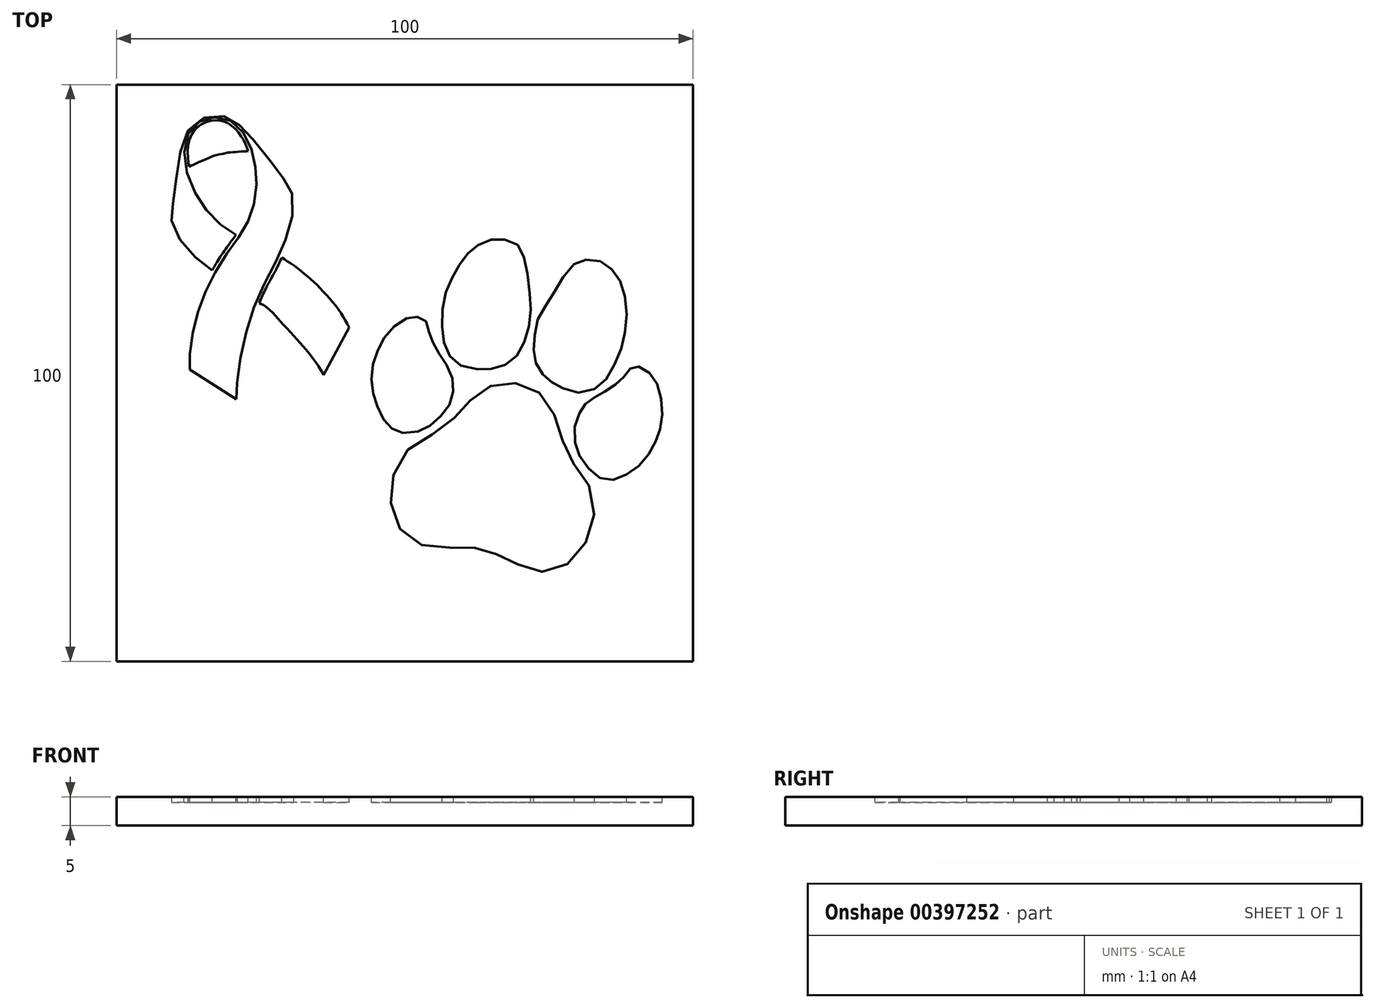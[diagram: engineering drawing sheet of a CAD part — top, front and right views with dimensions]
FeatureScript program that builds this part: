
annotation { "Feature Type Name" : "Feature", "Feature Type Description" : "" }
export const myFeature = defineFeature(function(context is Context, id is Id, definition is map)
    precondition{}
    {
        {
            var Q0;
            Q0=qCreatedBy(makeId("Top.planeOp"),FACE);
            var sketch = newSketch(context, id + "F0", { "sketchPlane" : qUnion([Q0])});
            skLineSegment(sketch, "E0.bottom", {"start": v(0, 0) * mm, "end": v(-100, 0) * mm});
            skLineSegment(sketch, "E0.top", {"start": v(0, 100) * mm, "end": v(-100, 100) * mm});
            skLineSegment(sketch, "E0.left", {"start": v(0, 0) * mm, "end": v(0, 100) * mm});
            skLineSegment(sketch, "E0.right", {"start": v(-100, 0) * mm, "end": v(-100, 100) * mm});
            skSolve(sketch);
        }
        {
            var Q0;
            Q0 = qSketchRegion(id + "F0", true);
            extrude(context, id + "F1", {"entities" : qUnion([Q0]), "depth" : 5 * mm});
        }
        {
            var Q0;
            Q0=makeQuery(id+"F1.opExtrude","CAP_FACE",FACE,{"disambiguationData":[OSD([sQuery(id+"F0.wireOp",EDGE,"E0.bottom"),sQuery(id+"F0.wireOp",EDGE,"E0.top"),sQuery(id+"F0.wireOp",EDGE,"E0.left"),sQuery(id+"F0.wireOp",EDGE,"E0.right")])],"isStart":false});
            var sketch = newSketch(context, id + "F2", { "sketchPlane" : qUnion([Q0])});
            skFitSpline(sketch, "E1", {"points": [v(-50.29, 39.62) * mm, v(-51.72, 39.96) * mm, v(-52.71, 40.84) * mm, v(-53.7, 41.94) * mm, v(-54.59, 43.82) * mm, v(-55.14, 45.36) * mm, v(-55.58, 46.9) * mm, v(-55.8, 49) * mm, v(-55.58, 51.1) * mm, v(-55.03, 53.09) * mm, v(-54.26, 54.85) * mm, v(-53.15, 56.62) * mm, v(-51.72, 58.17) * mm, v(-49.95, 59.38) * mm, v(-48.63, 59.71) * mm, v(-47.75, 59.71) * mm, v(-46.75, 59.38) * mm, v(-46.2, 58.72) * mm, v(-45.87, 57.61) * mm, v(-45.65, 56.4) * mm, v(-45.1, 55.3) * mm, v(-44.33, 53.86) * mm, v(-43.55, 52.65) * mm, v(-42.56, 51.1) * mm, v(-41.79, 49.23) * mm, v(-41.57, 47.57) * mm, v(-41.79, 45.92) * mm, v(-42.45, 44.15) * mm, v(-43.66, 42.6) * mm, v(-44.99, 41.28) * mm, v(-46.75, 40.29) * mm, v(-48.08, 39.73) * mm, v(-50.29, 39.62) * mm]});
            skFitSpline(sketch, "E2", {"points": [v(-37.37, 50.66) * mm, v(-35.83, 50.55) * mm, v(-34.5, 50.88) * mm, v(-32.85, 51.32) * mm, v(-31.41, 52.2) * mm, v(-30.09, 53.53) * mm, v(-29.32, 55.3) * mm, v(-28.65, 57.28) * mm, v(-28.21, 59.5) * mm, v(-28.21, 61.7) * mm, v(-28.32, 63.8) * mm, v(-28.65, 66.88) * mm, v(-29.1, 69.1) * mm, v(-29.76, 71.41) * mm, v(-30.42, 72.18) * mm, v(-31.74, 72.96) * mm, v(-33.29, 73.18) * mm, v(-34.72, 73.18) * mm, v(-36.27, 72.73) * mm, v(-37.6, 71.96) * mm, v(-38.7, 71.08) * mm, v(-39.69, 69.98) * mm, v(-40.57, 68.65) * mm, v(-41.35, 67.22) * mm, v(-42.34, 65.45) * mm, v(-43, 63.57) * mm, v(-43.44, 61.37) * mm, v(-43.55, 58.83) * mm, v(-43.44, 56.73) * mm, v(-43.11, 54.74) * mm, v(-42.45, 53.2) * mm, v(-41.12, 51.87) * mm, v(-39.8, 51.1) * mm, v(-37.37, 50.66) * mm]});
            skFitSpline(sketch, "E3", {"points": [v(-24.57, 48.45) * mm, v(-25.56, 49.23) * mm, v(-26.67, 50.66) * mm, v(-27.44, 52.2) * mm, v(-27.66, 54.2) * mm, v(-27.44, 56.51) * mm, v(-27, 59.05) * mm, v(-25.78, 61.37) * mm, v(-24.24, 63.8) * mm, v(-22.8, 66.22) * mm, v(-20.82, 68.76) * mm, v(-19.27, 69.53) * mm, v(-17.17, 69.64) * mm, v(-15.19, 68.87) * mm, v(-13.75, 67.55) * mm, v(-12.54, 65.67) * mm, v(-11.77, 62.91) * mm, v(-11.55, 59.5) * mm, v(-11.99, 56.07) * mm, v(-12.76, 53.42) * mm, v(-14.08, 50.66) * mm, v(-15.63, 48.23) * mm, v(-17.84, 46.9) * mm, v(-20.7, 46.69) * mm, v(-23.02, 47.57) * mm, v(-24.57, 48.45) * mm]});
            skFitSpline(sketch, "E4", {"points": [v(-19.71, 43.05) * mm, v(-20.38, 41.28) * mm, v(-20.6, 38.96) * mm, v(-20.15, 36.86) * mm, v(-19.5, 35.2) * mm, v(-17.95, 33.22) * mm, v(-16.4, 31.9) * mm, v(-14.86, 31.46) * mm, v(-12.98, 31.68) * mm, v(-11.1, 32.67) * mm, v(-9.45, 33.89) * mm, v(-8.01, 35.54) * mm, v(-6.8, 37.42) * mm, v(-6.25, 38.85) * mm, v(-5.7, 40.5) * mm, v(-5.37, 42.6) * mm, v(-5.48, 44.81) * mm, v(-5.92, 47.24) * mm, v(-6.8, 49) * mm, v(-7.8, 50.22) * mm, v(-9.17, 51.04) * mm, v(-9.89, 51.17) * mm, v(-10.6, 50.97) * mm, v(-11.4, 50.05) * mm, v(-11.99, 49.33) * mm, v(-12.64, 48.67) * mm, v(-13.9, 47.69) * mm, v(-15.2, 46.84) * mm, v(-16.38, 46.18) * mm, v(-17.43, 45.52) * mm, v(-18.42, 44.8) * mm, v(-19.14, 44.08) * mm, v(-19.71, 43.05) * mm]});
            skFitSpline(sketch, "E5", {"points": [v(-37.84, 19.69) * mm, v(-36.65, 19.43) * mm, v(-35.2, 18.92) * mm, v(-33.67, 18.41) * mm, v(-32.14, 17.65) * mm, v(-30.77, 16.96) * mm, v(-29.24, 16.28) * mm, v(-27.8, 15.77) * mm, v(-25.58, 15.52) * mm, v(-23.54, 15.94) * mm, v(-21.84, 16.88) * mm, v(-20.14, 18.33) * mm, v(-18.86, 20.2) * mm, v(-17.75, 22.84) * mm, v(-17.24, 24.88) * mm, v(-17.16, 27.43) * mm, v(-17.75, 29.73) * mm, v(-18.86, 31.77) * mm, v(-20.14, 33.47) * mm, v(-21.07, 34.75) * mm, v(-21.92, 36.37) * mm, v(-22.6, 38.24) * mm, v(-23.29, 40.54) * mm, v(-23.88, 42.24) * mm, v(-24.73, 44.2) * mm, v(-25.84, 45.82) * mm, v(-27.54, 47.18) * mm, v(-29.24, 47.94) * mm, v(-31.03, 48.28) * mm, v(-32.65, 48.37) * mm, v(-34.52, 47.94) * mm, v(-36.48, 47.18) * mm, v(-37.84, 46.07) * mm, v(-38.86, 44.96) * mm, v(-40.05, 43.69) * mm, v(-41.07, 42.58) * mm, v(-42.43, 41.3) * mm, v(-44.4, 39.86) * mm, v(-46, 39) * mm, v(-48.14, 37.82) * mm, v(-50.1, 35.94) * mm, v(-51.54, 33.65) * mm, v(-52.05, 31.86) * mm, v(-52.48, 29.48) * mm, v(-52.4, 27.43) * mm, v(-51.97, 25.4) * mm, v(-51.03, 23.26) * mm, v(-49.5, 21.65) * mm, v(-47.8, 20.45) * mm, v(-45.92, 19.86) * mm, v(-43.8, 19.69) * mm, v(-41.41, 19.77) * mm, v(-39.88, 19.94) * mm, v(-37.84, 19.69) * mm]});
            skLineSegment(sketch, "E6", {"start": v(-87.27, 50.56) * mm, "end": v(-79.23, 45.45) * mm});
            skFitSpline(sketch, "E7", {"points": [v(-87.4, 85.74) * mm, v(-87.52, 86.56) * mm, v(-87.64, 87.89) * mm, v(-87.56, 89.49) * mm, v(-87.13, 90.97) * mm, v(-86.58, 91.95) * mm, v(-85.96, 92.6) * mm, v(-85.22, 93.16) * mm, v(-84.24, 93.55) * mm, v(-83.23, 93.78) * mm, v(-82.02, 93.74) * mm, v(-81.12, 93.5) * mm, v(-80.38, 93.16) * mm, v(-79.75, 92.65) * mm, v(-79.09, 92.02) * mm, v(-78.47, 91.2) * mm, v(-77.96, 90.42) * mm, v(-77.57, 89.6) * mm, v(-77.37, 89.06) * mm, v(-77.18, 88.47) * mm], "startDerivative": vector(-2.44, 16.03) * mm, "endDerivative": vector(4.8, -14.41) * mm});
            skFitSpline(sketch, "E8", {"points": [v(-87.4, 85.74) * mm, v(-86.82, 86.05) * mm, v(-85.88, 86.48) * mm, v(-84.7, 87) * mm, v(-83.81, 87.38) * mm, v(-82.84, 87.73) * mm, v(-81.63, 88) * mm, v(-80.57, 88.24) * mm, v(-79.75, 88.28) * mm, v(-78.66, 88.4) * mm, v(-77.72, 88.43) * mm, v(-77.18, 88.47) * mm], "startDerivative": vector(7.32, 4.06) * mm, "endDerivative": vector(7.46, 0.67) * mm});
            skFitSpline(sketch, "E9", {"points": [v(-79.3, 73.96) * mm, v(-80.1, 74.36) * mm, v(-81.48, 75.33) * mm, v(-83.1, 76.74) * mm, v(-84.16, 77.9) * mm, v(-84.97, 78.97) * mm, v(-85.93, 80.49) * mm, v(-87.04, 82.56) * mm, v(-87.65, 84.33) * mm, v(-88.16, 86.36) * mm, v(-88.26, 87.98) * mm, v(-88.16, 89.6) * mm, v(-87.75, 91.01) * mm, v(-87.04, 92.38) * mm, v(-86.23, 93.14) * mm, v(-85.52, 93.64) * mm, v(-84.46, 94.1) * mm, v(-83.5, 94.3) * mm, v(-82.44, 94.35) * mm, v(-81.22, 94.15) * mm, v(-80.16, 93.75) * mm, v(-79.15, 92.99) * mm, v(-78.34, 92.08) * mm, v(-77.58, 90.96) * mm, v(-76.92, 89.75) * mm, v(-76.42, 88.23) * mm, v(-76.06, 86.66) * mm, v(-75.86, 85.4) * mm, v(-75.76, 84.23) * mm, v(-75.7, 82.81) * mm, v(-75.8, 81.3) * mm, v(-76.08, 79.66) * mm, v(-76.47, 78.14) * mm, v(-76.82, 77.04) * mm, v(-77.6, 75.45) * mm, v(-78.3, 74.24) * mm, v(-79.1, 73.13) * mm, v(-80.12, 71.76) * mm, v(-81.18, 70.3) * mm, v(-82.3, 68.52) * mm, v(-83.26, 66.7) * mm, v(-84.12, 65.03) * mm, v(-84.98, 63.06) * mm, v(-85.64, 61.18) * mm, v(-86.2, 59.41) * mm, v(-86.65, 57.6) * mm, v(-87, 55.52) * mm, v(-87.2, 53.8) * mm, v(-87.3, 52.14) * mm, v(-87.28, 51) * mm, v(-87.27, 50.56) * mm], "startDerivative": vector(-49.75, 22.47) * mm, "endDerivative": vector(0.94, -36.49) * mm});
            skFitSpline(sketch, "E10", {"points": [v(-79.3, 73.96) * mm, v(-79.8, 73.24) * mm, v(-80.03, 72.94) * mm, v(-80.38, 72.47) * mm, v(-80.96, 71.62) * mm, v(-81.72, 70.55) * mm, v(-82.42, 69.46) * mm, v(-82.85, 68.73) * mm, v(-83.14, 68.27) * mm, v(-83.4, 67.79) * mm], "startDerivative": vector(-4.69, -6.92) * mm, "endDerivative": vector(-2.87, -5.31) * mm});
            skFitSpline(sketch, "E11", {"points": [v(-83.4, 67.79) * mm, v(-84.54, 68.57) * mm, v(-86.16, 69.89) * mm, v(-87.98, 71.76) * mm, v(-89, 73.13) * mm, v(-89.9, 74.8) * mm, v(-90.4, 76.37) * mm, v(-90.46, 77.12) * mm, v(-90.3, 78.29) * mm, v(-90.1, 80.06) * mm, v(-89.8, 82.44) * mm, v(-89.4, 85.47) * mm, v(-88.94, 88.1) * mm, v(-88.49, 89.93) * mm, v(-87.63, 91.95) * mm, v(-86.61, 93.27) * mm, v(-84.98, 94.18) * mm, v(-83.4, 94.58) * mm, v(-81.86, 94.63) * mm, v(-80.54, 94.28) * mm, v(-79.53, 93.72) * mm, v(-78.47, 92.81) * mm, v(-77.5, 91.85) * mm, v(-76.19, 90.38) * mm, v(-74.32, 88.05) * mm, v(-73, 86.33) * mm, v(-71.63, 84.51) * mm, v(-70.77, 83.35) * mm, v(-69.96, 82.18) * mm, v(-69.61, 81.22) * mm, v(-69.36, 79.76) * mm, v(-69.46, 77.43) * mm, v(-70.02, 75) * mm, v(-70.88, 72.62) * mm, v(-71.74, 70.55) * mm, v(-72.65, 68.77) * mm, v(-73.91, 66.3) * mm, v(-75.18, 63.77) * mm, v(-76.04, 61.74) * mm, v(-76.9, 59.1) * mm, v(-77.57, 56.75) * mm, v(-78.27, 53.98) * mm, v(-78.77, 51.1) * mm, v(-79.1, 48.73) * mm, v(-79.1, 47.57) * mm, v(-79.18, 46.76) * mm, v(-79.23, 45.45) * mm], "startDerivative": vector(-59.22, 40.03) * mm, "endDerivative": vector(-0.04, -77.87) * mm});
            skLineSegment(sketch, "E12", {"start": v(-64.08, 49.64) * mm, "end": v(-59.66, 57.9) * mm});
            skFitSpline(sketch, "E13", {"points": [v(-64.08, 49.64) * mm, v(-64.85, 51) * mm, v(-67.06, 53.98) * mm, v(-68.94, 56.1) * mm, v(-71.4, 58.75) * mm, v(-72.77, 60.28) * mm, v(-74.47, 61.72) * mm, v(-75.23, 62.15) * mm], "startDerivative": vector(-5.18, 10.26) * mm, "endDerivative": vector(-5.94, 5.26) * mm});
            skFitSpline(sketch, "E14", {"points": [v(-59.66, 57.9) * mm, v(-60.6, 59.6) * mm, v(-61.79, 61.38) * mm, v(-63.57, 63.51) * mm, v(-65.2, 65.21) * mm, v(-66.9, 66.75) * mm, v(-68.51, 68.1) * mm, v(-70.13, 69.21) * mm, v(-71.32, 70) * mm], "startDerivative": vector(-7.58, 14.27) * mm, "endDerivative": vector(-11.08, 7.4) * mm});
            skFitSpline(sketch, "E15", {"points": [v(-71.32, 70) * mm, v(-71.68, 69.28) * mm, v(-72.04, 68.5) * mm, v(-72.67, 67.27) * mm, v(-73.18, 66.33) * mm, v(-73.82, 65.22) * mm, v(-74.27, 64.32) * mm, v(-74.63, 63.56) * mm, v(-74.93, 62.87) * mm, v(-75.23, 62.15) * mm], "startDerivative": vector(-3.64, -7.1) * mm, "endDerivative": vector(-1.08, -6.91) * mm});
            skSolve(sketch);
        }
        {
            var Q0;
            Q0=makeQuery(id+"F2.imprint","IMPRINT",FACE,{"disambiguationData":[TD([[makeQuery(id+"F2.imprint","IMPRINT",EDGE,{"derivedFrom":sQuery(id+"F2.wireOp",EDGE,"E12")}),1.0]])]});
            var Q1;
            Q1=makeQuery(id+"F2.imprint","IMPRINT",FACE,{"disambiguationData":[TD([[makeQuery(id+"F2.imprint","IMPRINT",EDGE,{"derivedFrom":sQuery(id+"F2.wireOp",EDGE,"E6")}),1.0]])]});
            var Q2;
            Q2=makeQuery(id+"F2.imprint","IMPRINT",FACE,{"disambiguationData":[TD([[makeQuery(id+"F2.imprint","IMPRINT",EDGE,{"derivedFrom":sQuery(id+"F2.wireOp",EDGE,"E7")}),-1.0]])]});
            var Q3;
            Q3=makeQuery(id+"F2.imprint","IMPRINT",FACE,{"disambiguationData":[TD([[makeQuery(id+"F2.imprint","IMPRINT",EDGE,{"derivedFrom":sQuery(id+"F2.wireOp",EDGE,"E1")}),-1.0]])]});
            var Q4;
            Q4=makeQuery(id+"F2.imprint","IMPRINT",FACE,{"disambiguationData":[TD([[makeQuery(id+"F2.imprint","IMPRINT",EDGE,{"derivedFrom":sQuery(id+"F2.wireOp",EDGE,"E2")}),1.0]])]});
            var Q5;
            Q5=makeQuery(id+"F2.imprint","IMPRINT",FACE,{"disambiguationData":[TD([[makeQuery(id+"F2.imprint","IMPRINT",EDGE,{"derivedFrom":sQuery(id+"F2.wireOp",EDGE,"E3")}),-1.0]])]});
            var Q6;
            Q6=makeQuery(id+"F2.imprint","IMPRINT",FACE,{"disambiguationData":[TD([[makeQuery(id+"F2.imprint","IMPRINT",EDGE,{"derivedFrom":sQuery(id+"F2.wireOp",EDGE,"E4")}),1.0]])]});
            var Q7;
            Q7=makeQuery(id+"F2.imprint","IMPRINT",FACE,{"disambiguationData":[TD([[makeQuery(id+"F2.imprint","IMPRINT",EDGE,{"derivedFrom":sQuery(id+"F2.wireOp",EDGE,"E5")}),1.0]])]});
            extrude(context, id + "F3", {"entities" : qUnion([Q0, Q1, Q2, Q3, Q4, Q5, Q6, Q7]), "operationType" : NewBodyOperationType.REMOVE, "oppositeDirection" : true, "depth" : 1 * mm});
        }
    });
